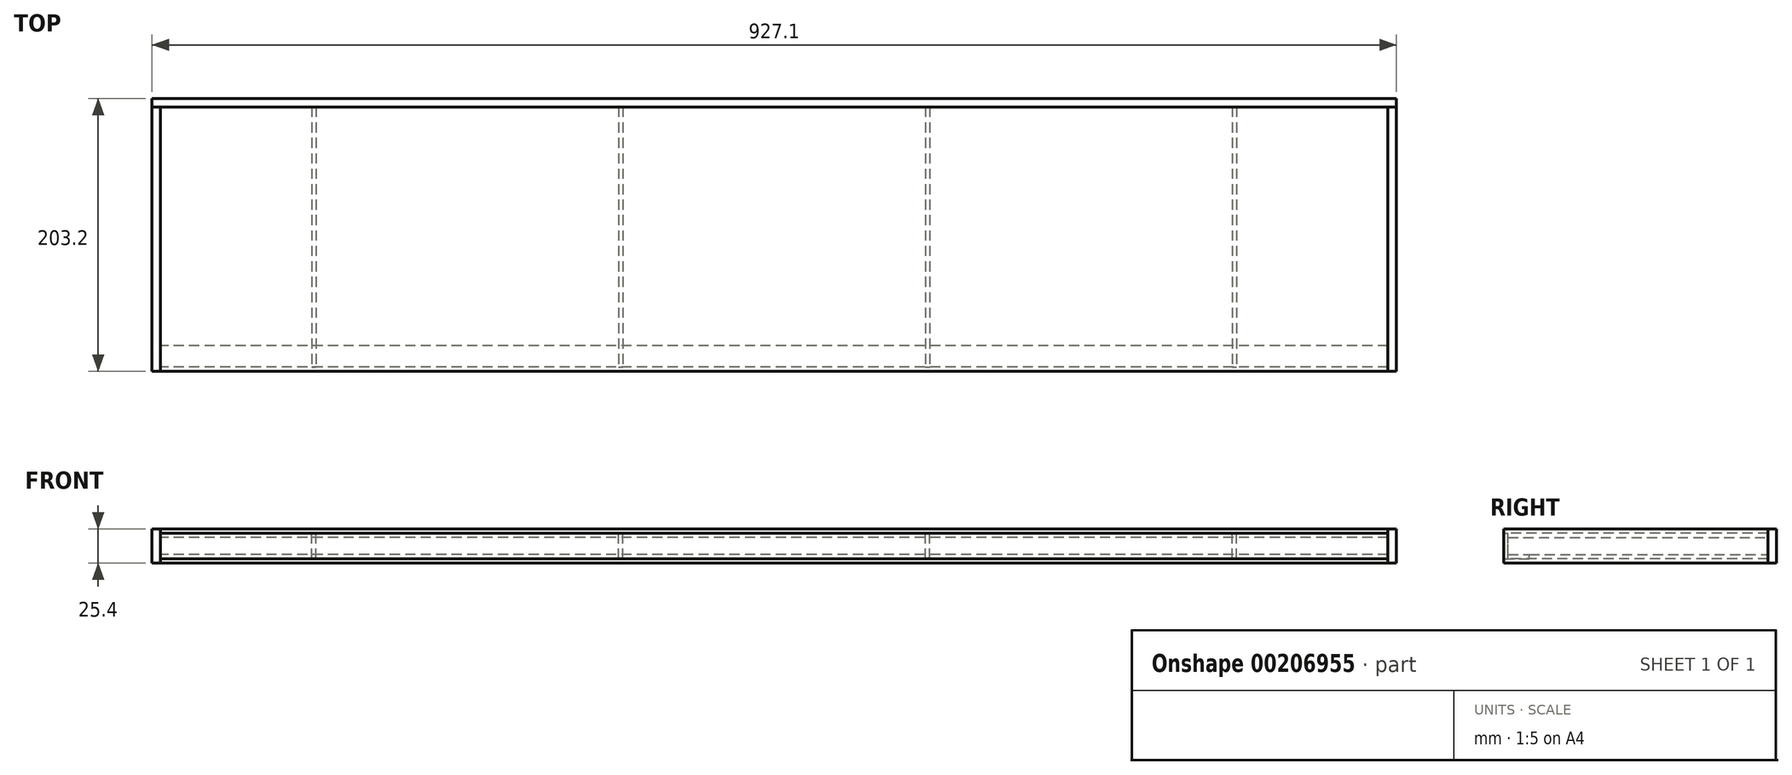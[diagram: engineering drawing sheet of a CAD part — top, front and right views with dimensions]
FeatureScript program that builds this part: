
annotation { "Feature Type Name" : "Feature", "Feature Type Description" : "" }
export const myFeature = defineFeature(function(context is Context, id is Id, definition is map)
    precondition{}
    {
        {
            var Q0;
            Q0=qCreatedBy(makeId("Right.planeOp"),FACE);
            var sketch = newSketch(context, id + "F0", { "sketchPlane" : qUnion([Q0])});
            skLineSegment(sketch, "E0.bottom", {"start": v(0, 0) * mm, "end": v(19.05, 0) * mm});
            skLineSegment(sketch, "E0.top", {"start": v(0, 19.05) * mm, "end": v(3.17, 19.05) * mm});
            skLineSegment(sketch, "E0.left", {"start": v(0, 0) * mm, "end": v(0, 19.05) * mm});
            skLineSegment(sketch, "E0.right", {"start": v(19.05, 0) * mm, "end": v(19.05, 3.18) * mm});
            skLineSegment(sketch, "E1.bottom", {"start": v(3.18, 3.17) * mm, "end": v(19.05, 3.18) * mm});
            skLineSegment(sketch, "E1.left", {"start": v(3.17, 3.18) * mm, "end": v(3.17, 19.05) * mm});
            skLineSegment(sketch, "E2.bottom", {"start": v(3.18, 3.18) * mm, "end": v(196.85, 3.18) * mm});
            skLineSegment(sketch, "E2.top", {"start": v(3.17, 15.87) * mm, "end": v(3.17, 15.87) * mm});
            skLineSegment(sketch, "E2.left", {"start": v(3.18, 3.18) * mm, "end": v(3.17, 15.87) * mm});
            skLineSegment(sketch, "E2.right", {"start": v(196.85, 3.18) * mm, "end": v(196.85, 15.88) * mm});
            skLineSegment(sketch, "E3", {"start": v(3.17, 19.05) * mm, "end": v(3.17, 15.87) * mm, "construction": true});
            skLineSegment(sketch, "E4.bottom", {"start": v(0, 22.23) * mm, "end": v(196.85, 22.23) * mm});
            skLineSegment(sketch, "E4.top", {"start": v(0, 15.87) * mm, "end": v(196.85, 15.88) * mm});
            skLineSegment(sketch, "E4.left", {"start": v(0, 22.23) * mm, "end": v(0, 19.05) * mm});
            skLineSegment(sketch, "E4.right", {"start": v(196.85, 22.23) * mm, "end": v(196.85, 15.88) * mm});
            skLineSegment(sketch, "E5.bottom", {"start": v(0, -3.17) * mm, "end": v(196.85, -3.17) * mm});
            skLineSegment(sketch, "E5.left", {"start": v(0, -3.17) * mm, "end": v(0, 0) * mm});
            skLineSegment(sketch, "E5.right", {"start": v(196.85, -3.17) * mm, "end": v(196.85, 3.18) * mm});
            skLineSegment(sketch, "E6.bottom", {"start": v(196.85, 22.23) * mm, "end": v(203.2, 22.23) * mm});
            skLineSegment(sketch, "E6.top", {"start": v(196.85, -3.17) * mm, "end": v(203.2, -3.17) * mm});
            skLineSegment(sketch, "E6.left", {"start": v(196.85, 22.23) * mm, "end": v(196.85, -3.17) * mm});
            skLineSegment(sketch, "E6.right", {"start": v(203.2, 22.23) * mm, "end": v(203.2, -3.17) * mm});
            skLineSegment(sketch, "E7", {"start": v(3.17, 15.87) * mm, "end": v(196.85, 15.88) * mm});
            skLineSegment(sketch, "E8", {"start": v(0, 19.05) * mm, "end": v(0, 15.88) * mm});
            skLineSegment(sketch, "E9", {"start": v(19.05, 3.18) * mm, "end": v(196.85, 3.18) * mm});
            skSolve(sketch);
        }
        {
            var Q0;
            Q0=makeQuery(id+"F0.imprint","IMPRINT",FACE,{"disambiguationData":[TD([[makeQuery(id+"F0.imprint","IMPRINT",EDGE,{"derivedFrom":sQuery(id+"F0.wireOp",EDGE,"E0.bottom")}),1.0]])]});
            var Q1;
            Q1=makeQuery(id+"F0.imprint","IMPRINT",FACE,{"disambiguationData":[TD([[makeQuery(id+"F0.imprint","IMPRINT",EDGE,{"derivedFrom":sQuery(id+"F0.wireOp",EDGE,"E0.top")}),-1.0]])]});
            extrude(context, id + "F1", {"entities" : qUnion([Q0, Q1]), "depth" : 914.4 * mm});
        }
        {
            var Q0;
            Q0=makeQuery(id+"F0.imprint","IMPRINT",FACE,{"disambiguationData":[TD([[makeQuery(id+"F0.imprint","IMPRINT",EDGE,{"derivedFrom":sQuery(id+"F0.wireOp",EDGE,"E0.top")}),1.0]])]});
            var Q1;
            Q1=makeQuery(id+"F0.imprint","IMPRINT",FACE,{"disambiguationData":[TD([[makeQuery(id+"F0.imprint","IMPRINT",EDGE,{"derivedFrom":sQuery(id+"F0.wireOp",EDGE,"E0.bottom")}),-1.0]])]});
            extrude(context, id + "F2", {"entities" : qUnion([Q0, Q1]), "depth" : 914.4 * mm});
        }
        {
            var Q0;
            {var subQ3=sQuery(id+"F0.wireOp",EDGE,"E6.bottom");Q0=makeQuery(id+"F0.imprint","IMPRINT",FACE,{"disambiguationData":[TD([[makeQuery(id+"F0.imprint","IMPRINT",EDGE,{"derivedFrom":subQ3}),-1.0]])]});}
            extrude(context, id + "F3", {"entities" : qUnion([Q0]), "depth" : 920.75 * mm, "hasSecondDirection" : true, "secondDirectionOppositeDirection" : true, "secondDirectionDepth" : 6.35 * mm});
        }
        {
            var Q0;
            Q0=qCreatedBy(makeId("Front.planeOp"),FACE);
            var sketch = newSketch(context, id + "F4", { "sketchPlane" : qUnion([Q0])});
            skLineSegment(sketch, "E10.bottom", {"start": v(0, -3.17) * mm, "end": v(-6.35, -3.17) * mm});
            skLineSegment(sketch, "E10.top", {"start": v(0, 22.23) * mm, "end": v(-6.35, 22.23) * mm});
            skLineSegment(sketch, "E10.left", {"start": v(0, -3.17) * mm, "end": v(0, 22.23) * mm});
            skLineSegment(sketch, "E10.right", {"start": v(-6.35, -3.17) * mm, "end": v(-6.35, 22.23) * mm});
            skLineSegment(sketch, "E11.bottom", {"start": v(914.4, -3.17) * mm, "end": v(920.75, -3.17) * mm});
            skLineSegment(sketch, "E11.top", {"start": v(914.4, 22.23) * mm, "end": v(920.75, 22.23) * mm});
            skLineSegment(sketch, "E11.left", {"start": v(914.4, -3.17) * mm, "end": v(914.4, 22.23) * mm});
            skLineSegment(sketch, "E11.right", {"start": v(920.75, -3.17) * mm, "end": v(920.75, 22.23) * mm});
            skSolve(sketch);
        }
        {
            var Q0;
            Q0=makeQuery(id+"F4.imprint","IMPRINT",FACE,{"disambiguationData":[TD([[makeQuery(id+"F4.imprint","IMPRINT",EDGE,{"derivedFrom":sQuery(id+"F4.wireOp",EDGE,"E11.bottom")}),1.0]])]});
            var Q1;
            Q1=makeQuery(id+"F4.imprint","IMPRINT",FACE,{"disambiguationData":[TD([[makeQuery(id+"F4.imprint","IMPRINT",EDGE,{"derivedFrom":sQuery(id+"F4.wireOp",EDGE,"E10.bottom")}),-1.0]])]});
            extrude(context, id + "F5", {"entities" : qUnion([Q0, Q1]), "endBound" : BoundingType.UP_TO_NEXT, "oppositeDirection" : true, "depth" : 25.4 * mm});
        }
        {
            var Q0;
            Q0=qCreatedBy(makeId("Front.planeOp"),FACE);
            cPlane(context, id + "F6", {"entities" : qUnion([Q0]), "cplaneType" : CPlaneType.OFFSET, "offset" : 3.25 * mm, "oppositeDirection" : true, "width" : 152.4 * mm, "height" : 152.4 * mm});
        }
        {
            var Q0;
            Q0=qCreatedBy(id+"F6.planeOp",FACE);
            var sketch = newSketch(context, id + "F7", { "sketchPlane" : qUnion([Q0])});
            skLineSegment(sketch, "E12.bottom", {"start": v(112.71, 0) * mm, "end": v(115.89, 0) * mm});
            skLineSegment(sketch, "E12.top", {"start": v(112.71, 19.05) * mm, "end": v(115.89, 19.05) * mm});
            skLineSegment(sketch, "E12.left", {"start": v(112.71, 0) * mm, "end": v(112.71, 19.05) * mm});
            skLineSegment(sketch, "E12.right", {"start": v(115.89, 0) * mm, "end": v(115.89, 19.05) * mm});
            skLineSegment(sketch, "E13.1.0.0", {"start": v(341.31, 19.05) * mm, "end": v(344.49, 19.05) * mm});
            skLineSegment(sketch, "E13.1.0.1", {"start": v(344.49, 0) * mm, "end": v(344.49, 19.05) * mm});
            skLineSegment(sketch, "E13.1.0.2", {"start": v(341.31, 0) * mm, "end": v(344.49, 0) * mm});
            skLineSegment(sketch, "E13.1.0.3", {"start": v(341.31, 0) * mm, "end": v(341.31, 19.05) * mm});
            skLineSegment(sketch, "E13.2.0.0", {"start": v(569.91, 19.05) * mm, "end": v(573.09, 19.05) * mm});
            skLineSegment(sketch, "E13.2.0.1", {"start": v(573.09, 0) * mm, "end": v(573.09, 19.05) * mm});
            skLineSegment(sketch, "E13.2.0.2", {"start": v(569.91, 0) * mm, "end": v(573.09, 0) * mm});
            skLineSegment(sketch, "E13.2.0.3", {"start": v(569.91, 0) * mm, "end": v(569.91, 19.05) * mm});
            skLineSegment(sketch, "E13.3.0.0", {"start": v(798.51, 19.05) * mm, "end": v(801.69, 19.05) * mm});
            skLineSegment(sketch, "E13.3.0.1", {"start": v(801.69, 0) * mm, "end": v(801.69, 19.05) * mm});
            skLineSegment(sketch, "E13.3.0.2", {"start": v(798.51, 0) * mm, "end": v(801.69, 0) * mm});
            skLineSegment(sketch, "E13.3.0.3", {"start": v(798.51, 0) * mm, "end": v(798.51, 19.05) * mm});
            skLineSegment(sketch, "E13.direction1", {"start": v(112.71, 0) * mm, "end": v(341.31, 0) * mm, "construction": true});
            skLineSegment(sketch, "E14", {"start": v(115.89, 0) * mm, "end": v(341.31, 0) * mm, "construction": true});
            skLineSegment(sketch, "E15", {"start": v(112.71, 0) * mm, "end": v(-112.71, 0) * mm, "construction": true});
            skPoint(sketch, "E16", {"position": v(0, 0) * mm});
            skLineSegment(sketch, "E17", {"start": v(801.69, 0) * mm, "end": v(1027.11, 0) * mm, "construction": true});
            skPoint(sketch, "E18", {"position": v(914.4, 0) * mm});
            skPoint(sketch, "E19", {"position": v(800.1, 19.05) * mm});
            skPoint(sketch, "E20", {"position": v(571.5, 19.05) * mm});
            skPoint(sketch, "E21", {"position": v(345.97, 33.95) * mm});
            skPoint(sketch, "E22", {"position": v(342.9, 19.05) * mm});
            skPoint(sketch, "E23", {"position": v(114.3, 19.05) * mm});
            skPoint(sketch, "E24", {"position": v(912.45, 19.68) * mm});
            skSolve(sketch);
        }
        {
            var Q0;
            Q0 = qSketchRegion(id + "F7", true);
            extrude(context, id + "F8", {"entities" : qUnion([Q0]), "oppositeDirection" : true, "depth" : 193.6 * mm});
        }
    });
